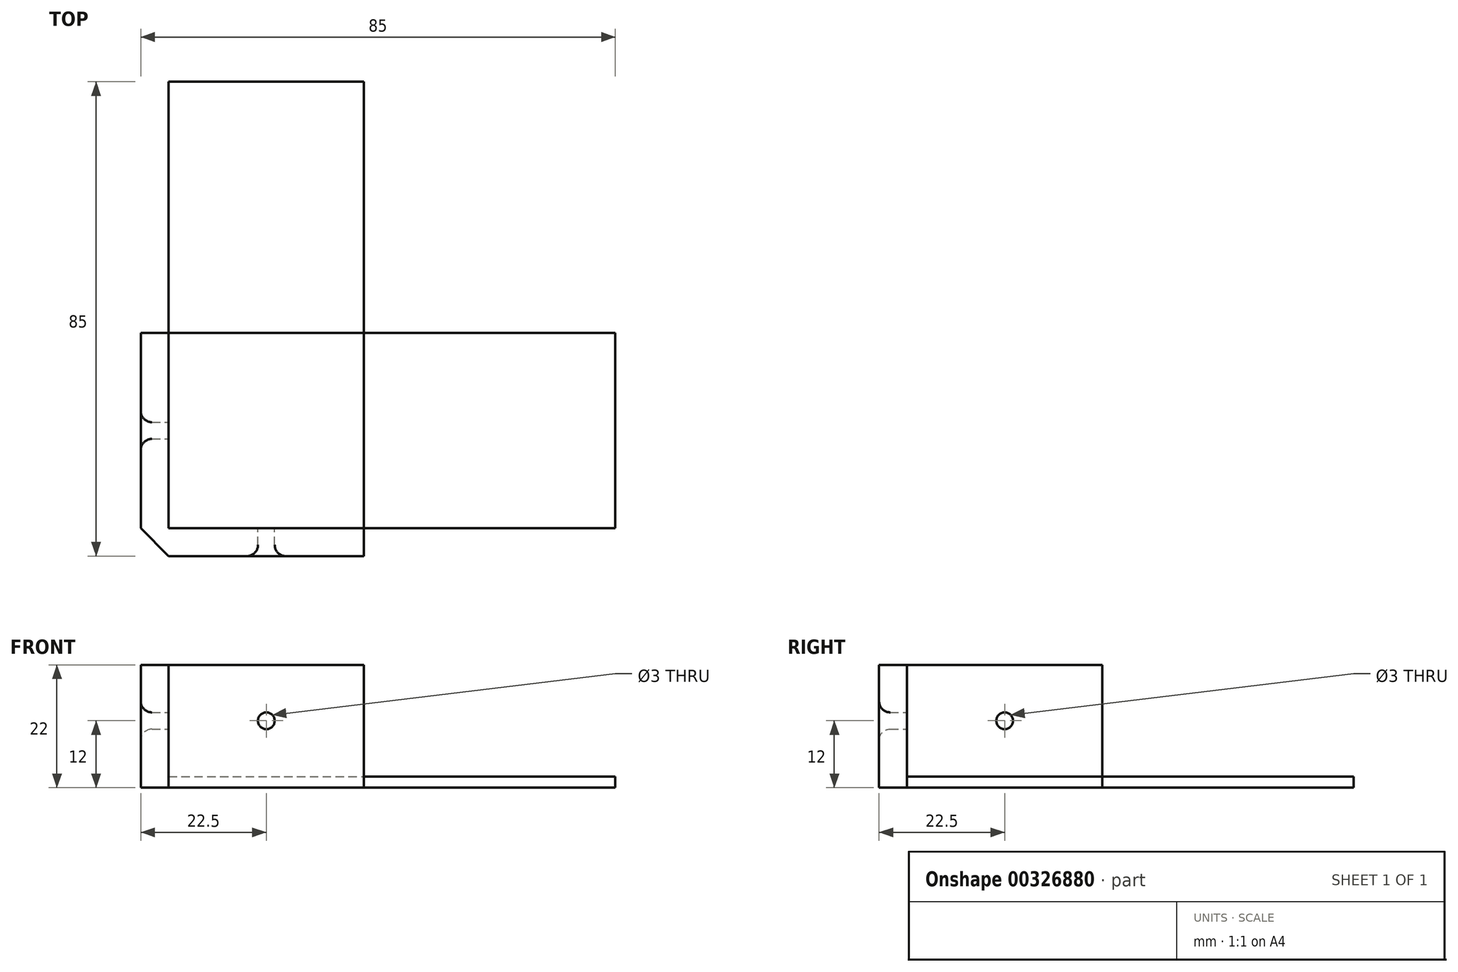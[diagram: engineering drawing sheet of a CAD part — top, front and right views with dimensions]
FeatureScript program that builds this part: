
annotation { "Feature Type Name" : "Feature", "Feature Type Description" : "" }
export const myFeature = defineFeature(function(context is Context, id is Id, definition is map)
    precondition{}
    {
        {
            var Q0;
            Q0=qCreatedBy(makeId("Top.planeOp"),FACE);
            var sketch = newSketch(context, id + "F0", { "sketchPlane" : qUnion([Q0])});
            skLineSegment(sketch, "E0.bottom", {"start": v(0, 0) * mm, "end": v(35, 0) * mm});
            skLineSegment(sketch, "E0.top", {"start": v(0, 80) * mm, "end": v(35, 80) * mm});
            skLineSegment(sketch, "E0.left", {"start": v(0, 0) * mm, "end": v(0, 80) * mm});
            skLineSegment(sketch, "E0.right", {"start": v(35, 0) * mm, "end": v(35, 80) * mm});
            skLineSegment(sketch, "E1.bottom", {"start": v(0, 0) * mm, "end": v(80, 0) * mm});
            skLineSegment(sketch, "E1.top", {"start": v(0, 35) * mm, "end": v(80, 35) * mm});
            skLineSegment(sketch, "E1.left", {"start": v(0, 0) * mm, "end": v(0, 35) * mm});
            skLineSegment(sketch, "E1.right", {"start": v(80, 0) * mm, "end": v(80, 35) * mm});
            skLineSegment(sketch, "E2.bottom", {"start": v(0, 0) * mm, "end": v(-5, 0) * mm});
            skLineSegment(sketch, "E2.top", {"start": v(0, 35) * mm, "end": v(-5, 35) * mm});
            skLineSegment(sketch, "E2.right", {"start": v(-5, 0) * mm, "end": v(-5, 35) * mm});
            skLineSegment(sketch, "E3.top", {"start": v(0, -5) * mm, "end": v(35, -5) * mm});
            skLineSegment(sketch, "E3.left", {"start": v(0, 0) * mm, "end": v(0, -5) * mm});
            skLineSegment(sketch, "E3.right", {"start": v(35, 0) * mm, "end": v(35, -5) * mm});
            skLineSegment(sketch, "E4", {"start": v(-5, 0) * mm, "end": v(0, -5) * mm});
            skSolve(sketch);
        }
        {
            var Q0;
            Q0=qCreatedBy(makeId("Front.planeOp"),FACE);
            var sketch = newSketch(context, id + "F1", { "sketchPlane" : qUnion([Q0])});
            skLineSegment(sketch, "E5.bottom", {"start": v(0, 0) * mm, "end": v(35, 0) * mm});
            skLineSegment(sketch, "E5.top", {"start": v(0, 20) * mm, "end": v(35, 20) * mm});
            skLineSegment(sketch, "E5.left", {"start": v(0, 0) * mm, "end": v(0, 20) * mm});
            skLineSegment(sketch, "E5.right", {"start": v(35, 0) * mm, "end": v(35, 20) * mm});
            skCircle(sketch, "E6", {"center": v(17.5, 10) * mm, "radius": 1.5 * mm});
            skPoint(sketch, "E6.centerSnap0", {"position": v(17.5, 20) * mm});
            skPoint(sketch, "E6.centerSnap1", {"position": v(0, 10) * mm});
            skSolve(sketch);
        }
        {
            var Q0;
            Q0=qCreatedBy(makeId("Right.planeOp"),FACE);
            var sketch = newSketch(context, id + "F2", { "sketchPlane" : qUnion([Q0])});
            skLineSegment(sketch, "E7.bottom", {"start": v(0, 0) * mm, "end": v(35, 0) * mm});
            skLineSegment(sketch, "E7.top", {"start": v(0, 20) * mm, "end": v(35, 20) * mm});
            skLineSegment(sketch, "E7.left", {"start": v(0, 0) * mm, "end": v(0, 20) * mm});
            skLineSegment(sketch, "E7.right", {"start": v(35, 0) * mm, "end": v(35, 20) * mm});
            skCircle(sketch, "E8", {"center": v(17.5, 10) * mm, "radius": 1.5 * mm});
            skPoint(sketch, "E8.centerSnap0", {"position": v(17.5, 20) * mm});
            skPoint(sketch, "E8.centerSnap1", {"position": v(35, 10) * mm});
            skSolve(sketch);
        }
        {
            var Q0;
            {var subQ0=sQuery(id+"F0.wireOp",EDGE,"E1.bottom");Q0=makeQuery(id+"F0.imprint","IMPRINT",FACE,{"disambiguationData":[TD([[makeQuery(id+"F0.imprint","IMPRINT",EDGE,{"derivedFrom":subQ0}),1.0]])]});}
            var Q1;
            {var subQ4=sQuery(id+"F0.wireOp",EDGE,"E1.left");Q1=makeQuery(id+"F0.imprint","IMPRINT",FACE,{"disambiguationData":[TD([[makeQuery(id+"F0.imprint","IMPRINT",EDGE,{"derivedFrom":subQ4}),-1.0]])]});}
            var Q2;
            {var subQ0=sQuery(id+"F0.wireOp",EDGE,"E0.top");Q2=makeQuery(id+"F0.imprint","IMPRINT",FACE,{"disambiguationData":[TD([[makeQuery(id+"F0.imprint","IMPRINT",EDGE,{"derivedFrom":subQ0}),-1.0]])]});}
            var Q3;
            Q3=makeQuery(id+"F0.imprint","IMPRINT",FACE,{"disambiguationData":[TD([[makeQuery(id+"F0.imprint","IMPRINT",EDGE,{"derivedFrom":sQuery(id+"F0.wireOp",EDGE,"E2.bottom")}),-1.0]])]});
            var Q4;
            Q4=makeQuery(id+"F0.imprint","IMPRINT",FACE,{"disambiguationData":[TD([[makeQuery(id+"F0.imprint","IMPRINT",EDGE,{"derivedFrom":sQuery(id+"F0.wireOp",EDGE,"E0.bottom")}),-1.0]])]});
            var Q5;
            Q5=makeQuery(id+"F0.imprint","IMPRINT",FACE,{"disambiguationData":[TD([[makeQuery(id+"F0.imprint","IMPRINT",EDGE,{"derivedFrom":sQuery(id+"F0.wireOp",EDGE,"E2.bottom")}),1.0]])]});
            extrude(context, id + "F3", {"entities" : qUnion([Q0, Q1, Q2, Q3, Q4, Q5]), "oppositeDirection" : true, "depth" : 2 * mm});
        }
        {
            var Q0;
            Q0=makeQuery(id+"F0.imprint","IMPRINT",FACE,{"disambiguationData":[TD([[makeQuery(id+"F0.imprint","IMPRINT",EDGE,{"derivedFrom":sQuery(id+"F0.wireOp",EDGE,"E2.bottom")}),1.0]])]});
            var Q1;
            Q1=makeQuery(id+"F0.imprint","IMPRINT",FACE,{"disambiguationData":[TD([[makeQuery(id+"F0.imprint","IMPRINT",EDGE,{"derivedFrom":sQuery(id+"F0.wireOp",EDGE,"E0.bottom")}),-1.0]])]});
            var Q2;
            Q2=makeQuery(id+"F0.imprint","IMPRINT",FACE,{"disambiguationData":[TD([[makeQuery(id+"F0.imprint","IMPRINT",EDGE,{"derivedFrom":sQuery(id+"F0.wireOp",EDGE,"E2.bottom")}),-1.0]])]});
            extrude(context, id + "F4", {"entities" : qUnion([Q0, Q1, Q2]), "operationType" : NewBodyOperationType.ADD, "depth" : 20 * mm});
        }
        {
            var Q0;
            Q0=makeQuery(id+"F1.imprint","IMPRINT",FACE,{"disambiguationData":[TD([[makeQuery(id+"F1.imprint","IMPRINT",EDGE,{"derivedFrom":sQuery(id+"F1.wireOp",EDGE,"E6")}),1.0]])]});
            extrude(context, id + "F5", {"entities" : qUnion([Q0]), "operationType" : NewBodyOperationType.REMOVE, "depth" : 25 * mm});
        }
        {
            var Q0;
            Q0=makeQuery(id+"F2.imprint","IMPRINT",FACE,{"disambiguationData":[TD([[makeQuery(id+"F2.imprint","IMPRINT",EDGE,{"derivedFrom":sQuery(id+"F2.wireOp",EDGE,"E8")}),1.0]])]});
            extrude(context, id + "F6", {"entities" : qUnion([Q0]), "operationType" : NewBodyOperationType.REMOVE, "oppositeDirection" : true, "depth" : 25 * mm});
        }
        {
            var Q0;
            {var subQ0=sQuery(id+"F0.wireOp",EDGE,"E3.top");Q0=makeQuery(id+"F5.boolean.opBoolean","INTERSECT",EDGE,{"derivedFrom":[makeQuery(id+"F4.boolean.opBoolean","MERGE",FACE,{"derivedFrom":[makeQuery(id+"F3.opExtrude","SWEPT_FACE",FACE,{"disambiguationData":[OSD([subQ0])]}),makeQuery(id+"F4.opExtrude","SWEPT_FACE",FACE,{"disambiguationData":[OSD([subQ0])]})]}),makeQuery(id+"F5.opExtrude","SWEPT_FACE",FACE,{"disambiguationData":[OSD([sQuery(id+"F1.wireOp",EDGE,"E6")])]})]});}
            var Q1;
            {var subQ0=sQuery(id+"F0.wireOp",EDGE,"E2.right");Q1=makeQuery(id+"F6.boolean.opBoolean","INTERSECT",EDGE,{"derivedFrom":[makeQuery(id+"F4.boolean.opBoolean","MERGE",FACE,{"derivedFrom":[makeQuery(id+"F3.opExtrude","SWEPT_FACE",FACE,{"disambiguationData":[OSD([subQ0])]}),makeQuery(id+"F4.opExtrude","SWEPT_FACE",FACE,{"disambiguationData":[OSD([subQ0])]})]}),makeQuery(id+"F6.opExtrude","SWEPT_FACE",FACE,{"disambiguationData":[OSD([sQuery(id+"F2.wireOp",EDGE,"E8")])]})]});}
            fillet(context, id + "F7", {"entities" : qUnion([Q0, Q1]), "radius" : 2 * mm, "allowEdgeOverflow" : false});
        }
    });
